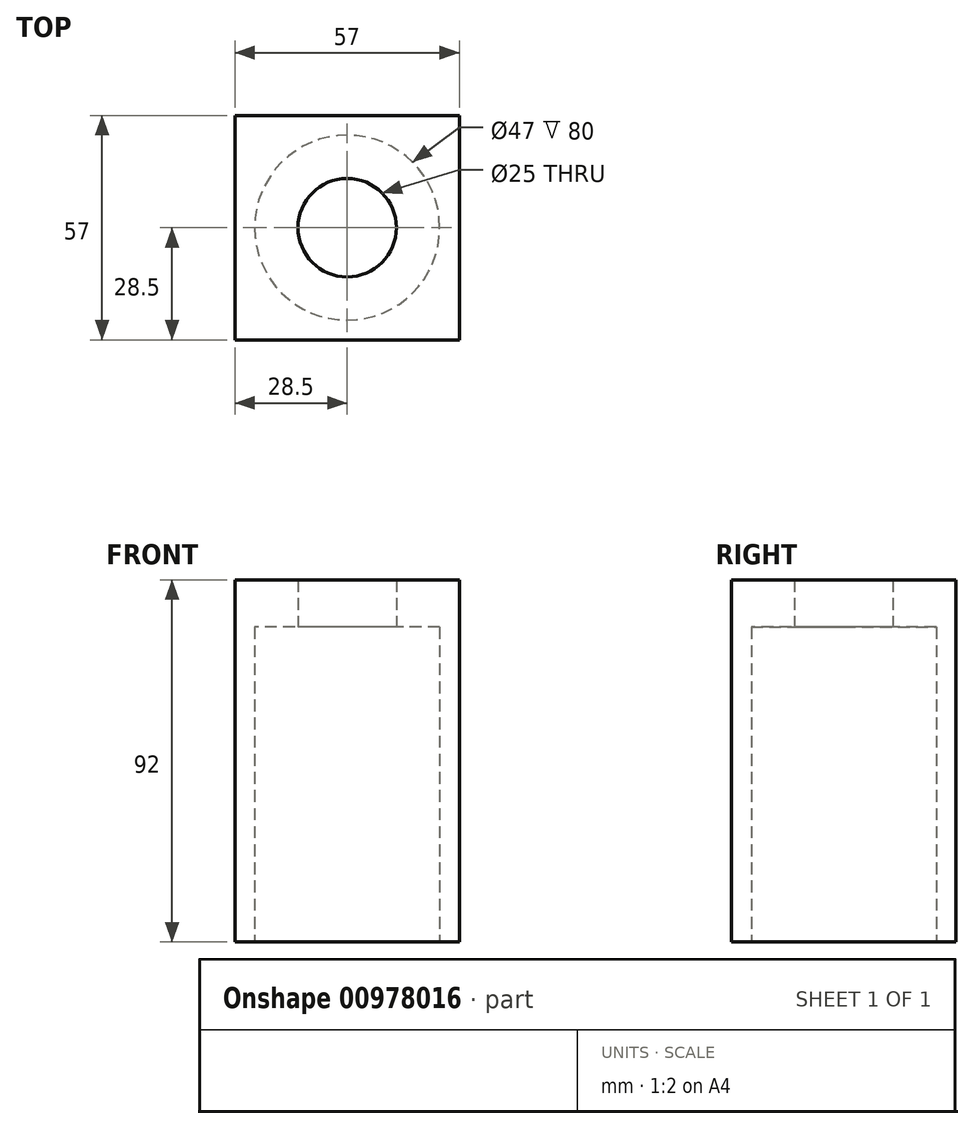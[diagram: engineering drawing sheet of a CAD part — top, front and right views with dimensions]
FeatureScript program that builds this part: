
annotation { "Feature Type Name" : "Feature", "Feature Type Description" : "" }
export const myFeature = defineFeature(function(context is Context, id is Id, definition is map)
    precondition{}
    {
        {
            var Q0;
            Q0=qCreatedBy(makeId("Top.planeOp"),FACE);
            var sketch = newSketch(context, id + "F0", { "sketchPlane" : qUnion([Q0])});
            skLineSegment(sketch, "E0.bottom", {"start": v(23.5, 23.5) * mm, "end": v(-23.5, 23.5) * mm});
            skLineSegment(sketch, "E0.top", {"start": v(23.5, -23.5) * mm, "end": v(-23.5, -23.5) * mm});
            skLineSegment(sketch, "E0.left", {"start": v(23.5, 23.5) * mm, "end": v(23.5, -23.5) * mm});
            skLineSegment(sketch, "E0.right", {"start": v(-23.5, 23.5) * mm, "end": v(-23.5, -23.5) * mm});
            skPoint(sketch, "E0.middle", {"position": v(0, 0) * mm});
            skLineSegment(sketch, "E1.bottom", {"start": v(-28.5, 28.5) * mm, "end": v(28.5, 28.5) * mm});
            skLineSegment(sketch, "E1.top", {"start": v(-28.5, -28.5) * mm, "end": v(28.5, -28.5) * mm});
            skLineSegment(sketch, "E1.left", {"start": v(-28.5, 28.5) * mm, "end": v(-28.5, -28.5) * mm});
            skLineSegment(sketch, "E1.right", {"start": v(28.5, 28.5) * mm, "end": v(28.5, -28.5) * mm});
            skCircle(sketch, "E2", {"center": v(0, 0) * mm, "radius": 23.5 * mm});
            skCircle(sketch, "E3", {"center": v(0, 0) * mm, "radius": 12.5 * mm});
            skSolve(sketch);
        }
        {
            var Q0;
            Q0 = qSketchRegion(id + "F0", true);
            var Q1;
            {var subQ0=sQuery(id+"F0.wireOp",EDGE,"E0.right");var subQ1=sQuery(id+"F0.wireOp",EDGE,"E0.bottom");var subQ2=makeQuery(id+"F0.imprint","INTERSECT",VERTEX,{"derivedFrom":[subQ1,subQ0]});Q1=makeQuery(id+"F0.imprint","IMPRINT",FACE,{"disambiguationData":[TD([[makeQuery(id+"F0.imprint","IMPRINT",EDGE,{"disambiguationData":[TD([[subQ2,1.0]])],"derivedFrom":subQ1}),1.0]])]});}
            var Q2;
            {var subQ0=sQuery(id+"F0.wireOp",EDGE,"E0.left");var subQ1=sQuery(id+"F0.wireOp",EDGE,"E0.bottom");var subQ2=makeQuery(id+"F0.imprint","INTERSECT",VERTEX,{"derivedFrom":[subQ1,subQ0]});Q2=makeQuery(id+"F0.imprint","IMPRINT",FACE,{"disambiguationData":[TD([[makeQuery(id+"F0.imprint","IMPRINT",EDGE,{"disambiguationData":[TD([[subQ2,-1.0]])],"derivedFrom":subQ1}),1.0]])]});}
            var Q3;
            {var subQ0=sQuery(id+"F0.wireOp",EDGE,"E0.left");var subQ1=sQuery(id+"F0.wireOp",EDGE,"E0.top");var subQ2=makeQuery(id+"F0.imprint","INTERSECT",VERTEX,{"derivedFrom":[subQ1,subQ0]});Q3=makeQuery(id+"F0.imprint","IMPRINT",FACE,{"disambiguationData":[TD([[makeQuery(id+"F0.imprint","IMPRINT",EDGE,{"disambiguationData":[TD([[subQ2,-1.0]])],"derivedFrom":subQ1}),-1.0]])]});}
            var Q4;
            {var subQ0=sQuery(id+"F0.wireOp",EDGE,"E0.right");var subQ1=sQuery(id+"F0.wireOp",EDGE,"E0.top");var subQ2=makeQuery(id+"F0.imprint","INTERSECT",VERTEX,{"derivedFrom":[subQ1,subQ0]});Q4=makeQuery(id+"F0.imprint","IMPRINT",FACE,{"disambiguationData":[TD([[makeQuery(id+"F0.imprint","IMPRINT",EDGE,{"disambiguationData":[TD([[subQ2,1.0]])],"derivedFrom":subQ1}),-1.0]])]});}
            var Q5;
            Q5=makeQuery(id+"F0.imprint","IMPRINT",FACE,{"disambiguationData":[TD([[makeQuery(id+"F0.imprint","IMPRINT",EDGE,{"derivedFrom":sQuery(id+"F0.wireOp",EDGE,"E3")}),-1.0]])]});
            var Q6;
            Q6=makeQuery(id+"F0.imprint","IMPRINT",FACE,{"disambiguationData":[TD([[makeQuery(id+"F0.imprint","IMPRINT",EDGE,{"derivedFrom":sQuery(id+"F0.wireOp",EDGE,"E3")}),1.0]])]});
            extrude(context, id + "F1", {"entities" : qUnion([Q0, Q1, Q2, Q3, Q4, Q5, Q6]), "depth" : 92 * mm, "offsetDistance" : 25 * mm});
        }
        {
            var Q0;
            Q0=makeQuery(id+"F0.imprint","IMPRINT",FACE,{"disambiguationData":[TD([[makeQuery(id+"F0.imprint","IMPRINT",EDGE,{"derivedFrom":sQuery(id+"F0.wireOp",EDGE,"E3")}),-1.0]])]});
            var Q1;
            Q1=makeQuery(id+"F0.imprint","IMPRINT",FACE,{"disambiguationData":[TD([[makeQuery(id+"F0.imprint","IMPRINT",EDGE,{"derivedFrom":sQuery(id+"F0.wireOp",EDGE,"E3")}),1.0]])]});
            extrude(context, id + "F2", {"entities" : qUnion([Q0, Q1]), "operationType" : NewBodyOperationType.REMOVE, "depth" : 80 * mm, "offsetDistance" : 25 * mm});
        }
        {
            var Q0;
            Q0=makeQuery(id+"F0.imprint","IMPRINT",FACE,{"disambiguationData":[TD([[makeQuery(id+"F0.imprint","IMPRINT",EDGE,{"derivedFrom":sQuery(id+"F0.wireOp",EDGE,"E3")}),1.0]])]});
            extrude(context, id + "F3", {"entities" : qUnion([Q0]), "operationType" : NewBodyOperationType.REMOVE, "endBound" : BoundingType.THROUGH_ALL, "depth" : 25 * mm, "offsetDistance" : 25 * mm});
        }
    });
